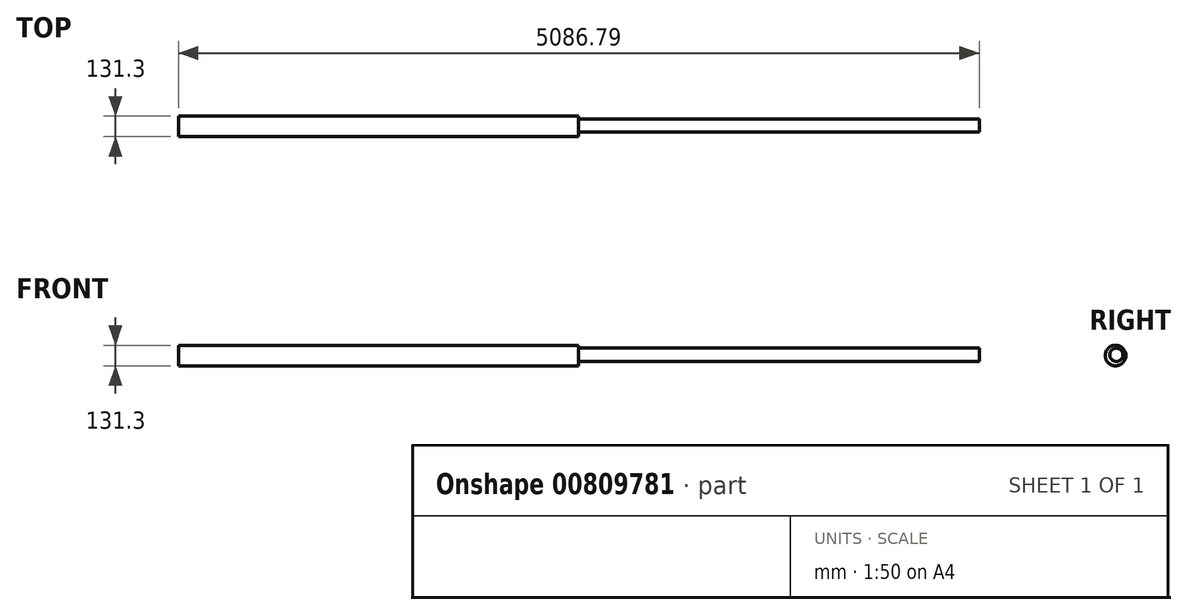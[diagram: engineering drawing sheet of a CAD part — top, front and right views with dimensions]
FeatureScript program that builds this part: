
annotation { "Feature Type Name" : "Feature", "Feature Type Description" : "" }
export const myFeature = defineFeature(function(context is Context, id is Id, definition is map)
    precondition{}
    {
        {
            var Q0;
            Q0=qCreatedBy(makeId("Right.planeOp"),FACE);
            var sketch = newSketch(context, id + "F0", { "sketchPlane" : qUnion([Q0])});
            skCircle(sketch, "E0", {"center": v(0, 0) * mm, "radius": 65.65 * mm});
            skSolve(sketch);
        }
        {
            var Q0;
            Q0 = qSketchRegion(id + "F0", true);
            extrude(context, id + "F1", {"entities" : qUnion([Q0]), "endBound" : BoundingType.SYMMETRIC, "depth" : 2540 * mm, "offsetDistance" : 25.4 * mm});
        }
        {
            var Q0;
            Q0=makeQuery(id+"F1.opExtrude","CAP_FACE",FACE,{"disambiguationData":[OSD([sQuery(id+"F0.wireOp",EDGE,"E0")])],"isStart":false});
            var sketch = newSketch(context, id + "F2", { "sketchPlane" : qUnion([Q0])});
            skCircle(sketch, "E1", {"center": v(5.34, 5.1) * mm, "radius": 42.27 * mm});
            skSolve(sketch);
        }
        {
            var Q0;
            Q0 = qSketchRegion(id + "F2", true);
            extrude(context, id + "F3", {"entities" : qUnion([Q0]), "operationType" : NewBodyOperationType.ADD, "endBound" : BoundingType.THROUGH_ALL, "depth" : 25.4 * mm, "offsetDistance" : 25.4 * mm});
        }
    });
